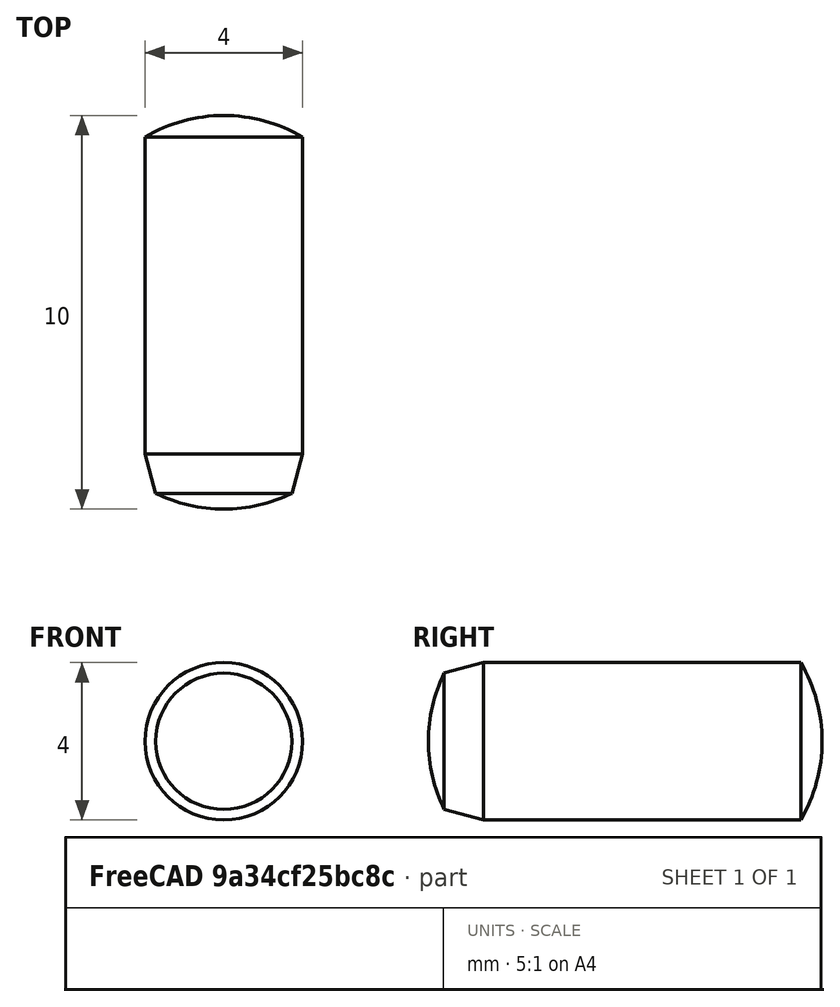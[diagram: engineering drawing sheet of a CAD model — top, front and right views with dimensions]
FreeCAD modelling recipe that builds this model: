
FCSTD DOCUMENT  (FreeCAD 0.15R4470 (Git))
Label: Zyl-Stift_DIN_6325-4x10
License: CC-BY 3.0
LicenseURL: http://creativecommons.org/licenses/by/3.0/
objects: Sketcher::SketchObject×1, PartDesign::Revolution×1
note: 3 computed .brp shape members not serialized (recipe doc carries the construction recipe); baked Part::Feature solids carry a one-line shape summary decoded from their .brp

FEATURE [Sketcher::SketchObject] Sketch
  Placement = pos=(0,0,0) rot=(0.57735,0.57735,0.57735;2.0944rad)
  sketch-geometry (5):
    g0: ArcOfCircle CenterX=3.55 CenterY=0 CenterZ=0 NormalX=0 NormalY=0 NormalZ=1 Radius=3.95 StartAngle=2.68767 EndAngle=3.14159
    g1: LineSegment StartX=0 StartY=1.73205 StartZ=0 EndX=1 EndY=2 EndZ=0
    g2: LineSegment StartX=1 StartY=2 StartZ=0 EndX=9.05624 EndY=2 EndZ=0
    g3: ArcOfCircle CenterX=5.65 CenterY=0 CenterZ=0 NormalX=0 NormalY=0 NormalZ=1 Radius=3.95 StartAngle=0 EndAngle=0.530923
    g4: LineSegment StartX=-0.4 StartY=0 StartZ=0 EndX=9.6 EndY=0 EndZ=0
  constraints (17):
    c: PointOnObject(g0,g-1)
    c: PointOnObject(g0,g-1)
    c: PointOnObject(g0,g-2)
    c: Coincident(g0,g1)
    c: Coincident(g1,g2)
    c: Horizontal(g2)
    c: PointOnObject(g3,g-1)
    c: Coincident(g3,g2)
    c: PointOnObject(g3,g-1)
    c: Coincident(g4,g0)
    c: Coincident(g4,g3)
    c: Equal(g0,g3)
    c: Angle(g4,g1) = 0.261799
    c: DistanceX(g4) = 10
    c: DistanceY(g-1,g1) = 2
    c: DistanceX(g1) = 1
    c: DistanceX(g0,g0) = 0.4
FEATURE [PartDesign::Revolution] Revolution  label="Zyl-Stift DIN 6325-4x10 #"
  Angle = 360
  Axis = (0,1,0)
  Base = (0,0,0)
  Placement = pos=(0,0,0) rot=(0.57735,0.57735,0.57735;2.0944rad)
  ReferenceAxis = -> Sketch [H_Axis]
  Sketch = -> Sketch
